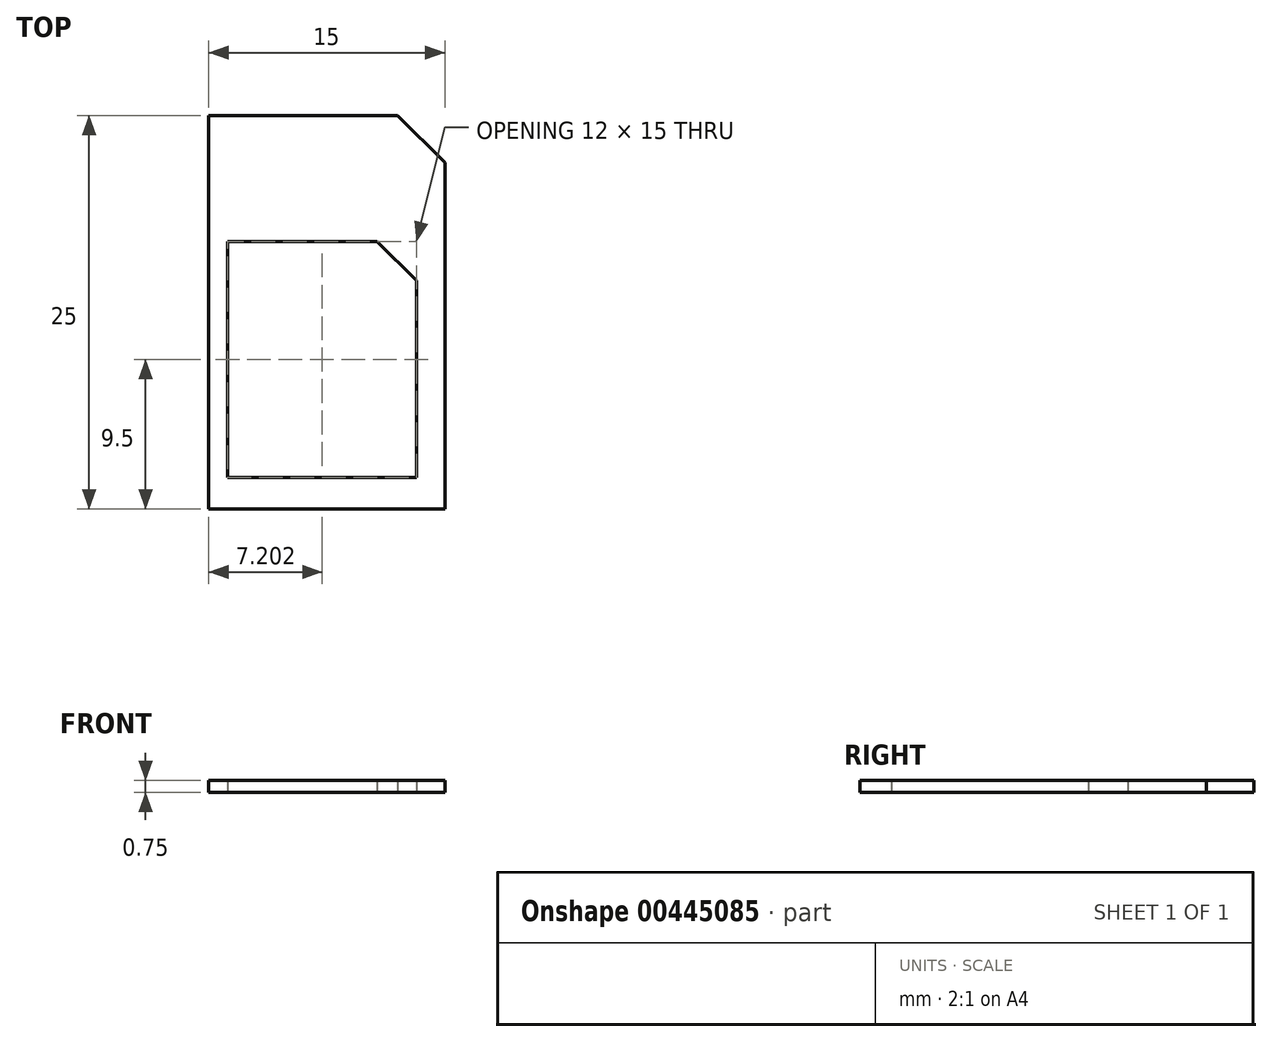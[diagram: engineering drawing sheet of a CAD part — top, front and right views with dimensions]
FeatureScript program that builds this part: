
annotation { "Feature Type Name" : "Feature", "Feature Type Description" : "" }
export const myFeature = defineFeature(function(context is Context, id is Id, definition is map)
    precondition{}
    {
        {
            var Q0;
            Q0=qCreatedBy(makeId("Top.planeOp"),FACE);
            var sketch = newSketch(context, id + "F0", { "sketchPlane" : qUnion([Q0])});
            skLineSegment(sketch, "E0.bottom", {"start": v(-32.09, -22) * mm, "end": v(-17.09, -22) * mm});
            skLineSegment(sketch, "E0.top", {"start": v(-32.09, 3) * mm, "end": v(-20.09, 3) * mm});
            skLineSegment(sketch, "E0.left", {"start": v(-32.09, -22) * mm, "end": v(-32.09, 3) * mm});
            skLineSegment(sketch, "E0.right", {"start": v(-17.09, -22) * mm, "end": v(-17.09, 0) * mm});
            skLineSegment(sketch, "E1", {"start": v(-20.09, 3) * mm, "end": v(-17.09, 0) * mm});
            skLineSegment(sketch, "E2.bottom", {"start": v(-30.89, -20) * mm, "end": v(-18.89, -20) * mm});
            skLineSegment(sketch, "E2.top", {"start": v(-30.89, -5) * mm, "end": v(-21.39, -5) * mm});
            skLineSegment(sketch, "E2.left", {"start": v(-30.89, -20) * mm, "end": v(-30.89, -5) * mm});
            skLineSegment(sketch, "E2.right", {"start": v(-18.89, -20) * mm, "end": v(-18.89, -7.5) * mm});
            skLineSegment(sketch, "E3", {"start": v(-21.39, -5) * mm, "end": v(-18.89, -7.5) * mm});
            skSolve(sketch);
        }
        {
            var Q0;
            Q0=makeQuery(id+"F0.imprint","IMPRINT",FACE,{"disambiguationData":[TD([[makeQuery(id+"F0.imprint","IMPRINT",EDGE,{"derivedFrom":sQuery(id+"F0.wireOp",EDGE,"E0.bottom")}),1.0]])]});
            extrude(context, id + "F1", {"entities" : qUnion([Q0]), "depth" : 0.75 * mm});
        }
    });
